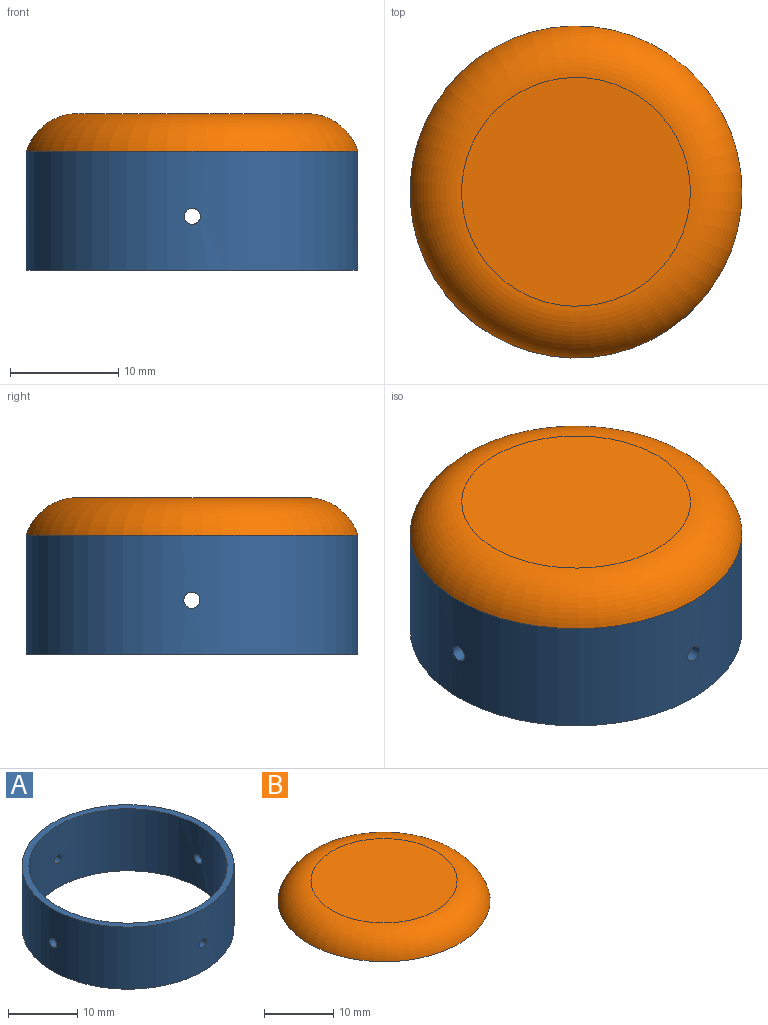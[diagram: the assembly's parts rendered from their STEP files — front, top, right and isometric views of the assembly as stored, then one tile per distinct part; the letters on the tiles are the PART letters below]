
ASSEMBLY  parts=2 mates=1
PART A: 8 faces, bbox 30.7x30.7x11 mm
  f0: cylinder r=14.35mm len=28.7mm, axis (0,0,-1), area 984.7mm2, adj f2,f3,f4,f5,f6,f7
  f1: cylinder r=15.35mm len=30.7mm, axis (0,0,-1), area 1053.9mm2, adj f2,f3,f4,f5,f6,f7
  f2: plane 30.7x30.7mm, normal (0,0,1), area 93.3mm2, adj f0,f1
  f3: plane 30.7x30.7mm, normal (0,0,-1), area 93.3mm2, adj f0,f1
  f4: cylinder r=0.75mm len=1.5mm, axis (1,0,0), area 4.7mm2, adj f0,f1
  f5: cylinder r=0.75mm len=1.5mm, axis (1,0,0), area 4.7mm2, adj f0,f1
  f6: cylinder r=0.75mm len=1.5mm, axis (0,-1,0), area 4.7mm2, adj f0,f1
  f7: cylinder r=0.75mm len=1.5mm, axis (0,-1,0), area 4.7mm2, adj f0,f1
PART B: 3 faces, bbox 33.7x33.7x5 mm
  f0: plane 30.7x30.7mm, normal (0,0,-1), area 740.2mm2, adj f2
  f1: plane 21.16x21.16mm, normal (0,0,1), area 351.7mm2, adj f2
  f2: torus R=10.58mm, axis (0,0,-1), area 530.8mm2, adj f0,f1
PLACE A t=(1,1.62,2.82)mm
PLACE B t=(1,1.62,17.32)mm
MATE fastened B.f2 <-> A.f1  axis (0,0,-1) through (1,1.62,13.82)mm
